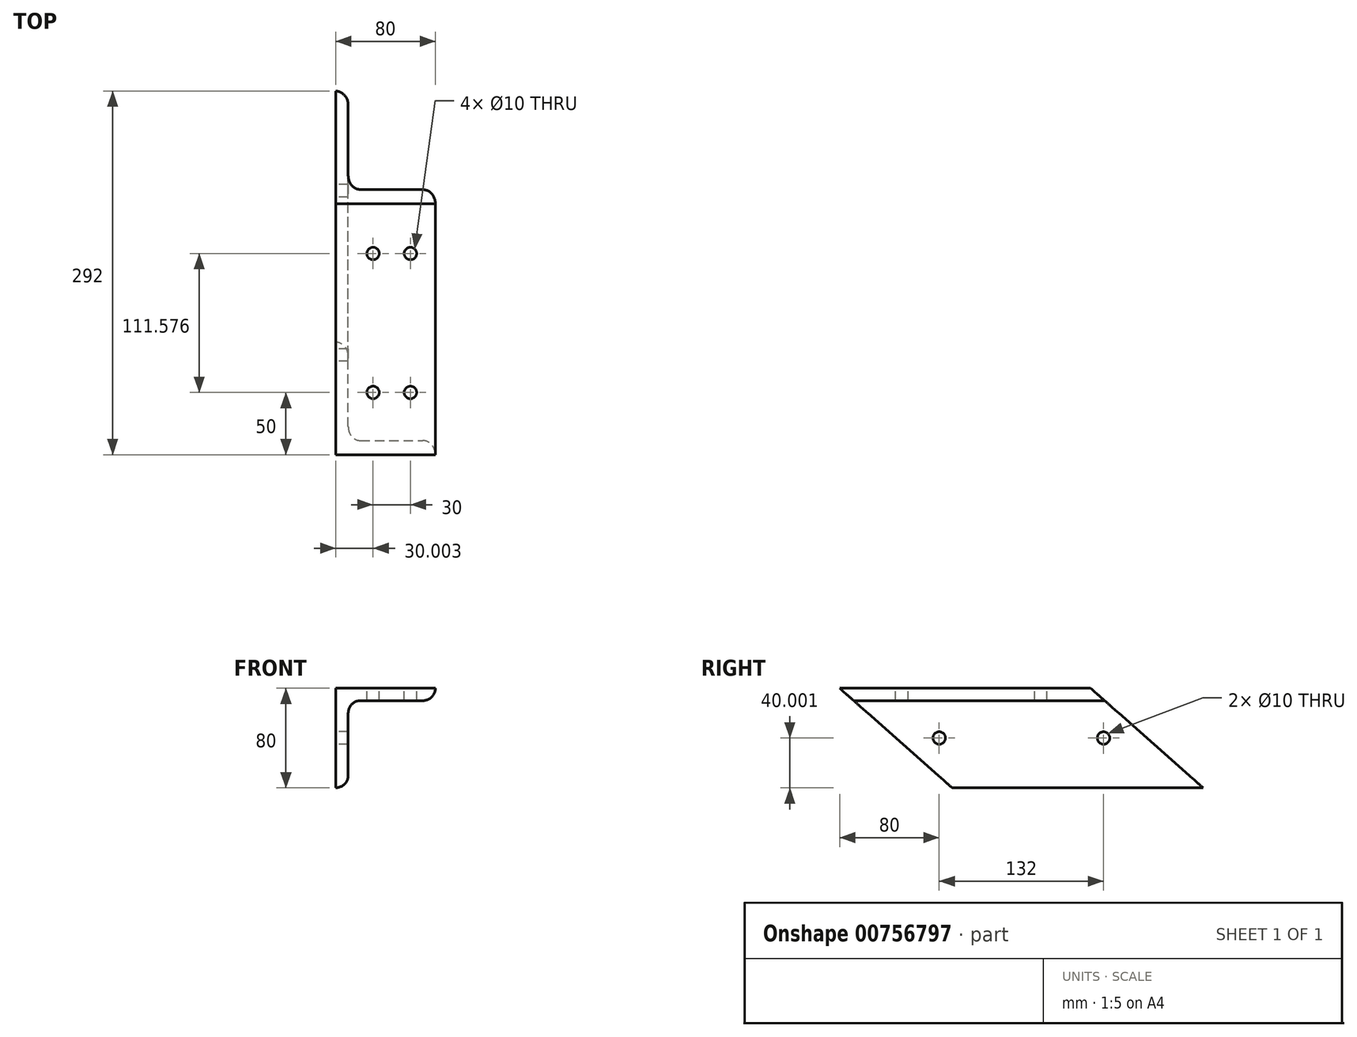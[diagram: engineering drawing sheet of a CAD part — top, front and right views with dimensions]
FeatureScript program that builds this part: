
annotation { "Feature Type Name" : "Feature", "Feature Type Description" : "" }
export const myFeature = defineFeature(function(context is Context, id is Id, definition is map)
    precondition{}
    {
        {
            var Q0;
            Q0=qCreatedBy(makeId("Front.planeOp"),FACE);
            var sketch = newSketch(context, id + "F0", { "sketchPlane" : qUnion([Q0])});
            skLineSegment(sketch, "E0.bottom", {"start": v(-90.88, 89.11) * mm, "end": v(-10.88, 89.11) * mm});
            skLineSegment(sketch, "E0.top", {"start": v(-90.88, 9.11) * mm, "end": v(-90.88, 9.11) * mm});
            skLineSegment(sketch, "E0.left", {"start": v(-90.88, 89.11) * mm, "end": v(-90.88, 9.11) * mm});
            skLineSegment(sketch, "E0.right", {"start": v(-10.88, 89.11) * mm, "end": v(-10.88, 89.11) * mm});
            skLineSegment(sketch, "E1.bottom", {"start": v(-10.88, 9.11) * mm, "end": v(-80.88, 9.11) * mm});
            skLineSegment(sketch, "E1.top", {"start": v(-20.88, 79.11) * mm, "end": v(-70.88, 79.11) * mm});
            skLineSegment(sketch, "E1.left", {"start": v(-10.88, 9.11) * mm, "end": v(-10.88, 79.11) * mm});
            skLineSegment(sketch, "E1.right", {"start": v(-80.88, 19.11) * mm, "end": v(-80.88, 69.11) * mm});
            skPoint(sketch, "E2.visualSharp", {"position": v(-80.88, 79.11) * mm});
            skArc(sketch, "E2.filletArc", {"start": v(-70.88, 79.11) * mm, "mid": v(-77.95, 76.18) * mm, "end": v(-80.88, 69.11) * mm});
            skArc(sketch, "E3.filletArc", {"start": v(-90.88, 9.11) * mm, "mid": v(-83.8, 12.04) * mm, "end": v(-80.88, 19.11) * mm});
            skArc(sketch, "E4.filletArc", {"start": v(-20.88, 79.11) * mm, "mid": v(-13.8, 82.04) * mm, "end": v(-10.88, 89.11) * mm});
            skSolve(sketch);
        }
        {
            var Q0;
            Q0=qSketchRegion(id+"F0",true);
            extrude(context, id + "F1", {"entities" : qUnion([Q0]), "depth" : 292 * mm, "offsetDistance" : 25 * mm});
        }
        {
            var Q0;
            Q0=makeQuery(id+"F1.opExtrude","SWEPT_FACE",FACE,{"disambiguationData":[OSD([sQuery(id+"F0.wireOp",EDGE,"E0.left")])]});
            var sketch = newSketch(context, id + "F2", { "sketchPlane" : qUnion([Q0])});
            skLineSegment(sketch, "E5", {"start": v(292, 89.11) * mm, "end": v(201.58, 9.11) * mm});
            skLineSegment(sketch, "E6", {"start": v(0, 9.11) * mm, "end": v(90.42, 89.11) * mm});
            skSolve(sketch);
        }
        {
            var Q0;
            {var subQ0=sQuery(id+"F2.wireOp",EDGE,"E5");Q0=makeQuery(id+"F2.imprint","IMPRINT",FACE,{"disambiguationData":[TD([[makeQuery(id+"F2.imprint","IMPRINT",EDGE,{"derivedFrom":subQ0}),1.0]])]});}
            var Q1;
            {var subQ0=sQuery(id+"F2.wireOp",EDGE,"E6");Q1=makeQuery(id+"F2.imprint","IMPRINT",FACE,{"disambiguationData":[TD([[makeQuery(id+"F2.imprint","IMPRINT",EDGE,{"derivedFrom":subQ0}),1.0]])]});}
            extrude(context, id + "F3", {"entities" : qUnion([Q0, Q1]), "operationType" : NewBodyOperationType.REMOVE, "oppositeDirection" : true, "depth" : 80 * mm, "offsetDistance" : 25 * mm});
        }
        {
            var Q0;
            Q0=makeQuery(id+"F1.opExtrude","SWEPT_FACE",FACE,{"disambiguationData":[OSD([sQuery(id+"F0.wireOp",EDGE,"E0.left")])]});
            var sketch = newSketch(context, id + "F4", { "sketchPlane" : qUnion([Q0])});
            skCircle(sketch, "E7", {"center": v(212, 49.11) * mm, "radius": 5 * mm});
            skCircle(sketch, "E8", {"center": v(80, 49.11) * mm, "radius": 5 * mm});
            skSolve(sketch);
        }
        {
            var Q0;
            Q0=qSketchRegion(id+"F4",true);
            extrude(context, id + "F5", {"entities" : qUnion([Q0]), "operationType" : NewBodyOperationType.REMOVE, "oppositeDirection" : true, "depth" : 25 * mm, "offsetDistance" : 25 * mm});
        }
        {
            var Q0;
            Q0=makeQuery(id+"F1.opExtrude","SWEPT_FACE",FACE,{"disambiguationData":[OSD([sQuery(id+"F0.wireOp",EDGE,"E0.bottom")])]});
            var sketch = newSketch(context, id + "F6", { "sketchPlane" : qUnion([Q0])});
            skCircle(sketch, "E9", {"center": v(-60.88, -242) * mm, "radius": 5 * mm});
            skCircle(sketch, "E10", {"center": v(-60.88, -130.42) * mm, "radius": 5 * mm});
            skCircle(sketch, "E11", {"center": v(-30.88, -130.42) * mm, "radius": 5 * mm});
            skCircle(sketch, "E12", {"center": v(-30.88, -242) * mm, "radius": 5 * mm});
            skSolve(sketch);
        }
        {
            var Q0;
            Q0=qSketchRegion(id+"F6",true);
            extrude(context, id + "F7", {"entities" : qUnion([Q0]), "operationType" : NewBodyOperationType.REMOVE, "oppositeDirection" : true, "depth" : 25 * mm, "offsetDistance" : 25 * mm});
        }
    });
